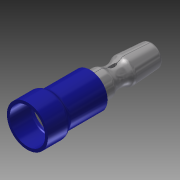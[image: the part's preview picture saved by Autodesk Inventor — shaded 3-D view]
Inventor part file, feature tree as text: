
AUTODESK INVENTOR PART (.ipt)
format: ipt  version: 2014 (Build 180170000, 170)  size: 401,408 bytes
history: native  units: in
note: dims shown in document units (in); Inventor stores cm internally (conversion verified against a paired STEP export)
features: sketch x7, projected_geometry x7, extrude x5, fillet x4, shell x2, revolve x2, plane x1, chamfer x1
ambient origin geometry x8: Origin, YZ Plane, XZ Plane, XY Plane, X Axis, Y Axis, Z Axis, Center Point
bodies: Solid1 (feature_tree), Solid2 (feature_tree)
feature tree (29):
  extrude  "Extrusion1"  Depth=0.375in TaperAngle=0.0deg
  extrude  "Extrusion2"  Depth=0.131in TaperAngle=0.0deg
  fillet  "Fillet1"  Radius=0.03in
  shell  "Shell1"  Thickness=0.017in
  revolve  "Revolution1"  Angle=90.0deg
  revolve  "Revolution2"  [1 undecoded]
  shell  "Shell2"  Thickness=0.13in
  fillet  "Fillet2"  Radius=0.179in
  fillet  "Fillet3"  Radius=0.075in
  extrude  "Extrusion3"  TaperAngle=90.0deg  [1 undecoded]
  extrude  "Extrusion4"  Depth=0.03in
  plane  "Work Plane1"
  extrude  "Extrusion5"  TaperAngle=0.0deg  [1 undecoded]
  fillet  "Fillet4"  Radius=0.002in
  chamfer  "Chamfer1"  Distance=0.0625in
  sketch  "Sketch1"  dims[d0=0.208in d1=0.375in d2=0.0in]
  sketch  "Sketch2"  dims[d3=0.245in d4=0.131in d5=0.0in d6=0.03in d7=0.017in]
  projected_geometry  "Projected Loop1"
  sketch  "Sketch3"  dims[d8=0.029in d9=90.0deg]
  sketch  "Sketch4"  dims[d10=0.373in d11=0.1525in d12=0.13in d13=0.179in d14=0.075in]
  sketch  "Sketch6"  dims[d15=0.1in d16=90.0deg]
  sketch  "Sketch7"  dims[d19=0.029in d20=0.03in]
  sketch  "Sketch8"  dims[d21=0.02in d22=0.0in d23=0.0in d24=0.002in d25=0.0in d26=0.0625in d27=0.11in d28=-0.055in d29=0.0075in d30=0.003in d31=0.125in d32=45.0deg]
  projected_geometry  "Projected Loop3"
  projected_geometry  "Project Cut Edges1"
  projected_geometry  "Project Cut Edges2"
  projected_geometry  "Project Cut Edges3"
  projected_geometry  "Project Cut Edges4"
  projected_geometry  "Project Cut Edges5"
note: 3 required parameter values undecoded (feature->parameter linkage not recoverable at this tier; creation-order binding heuristic only, values carry confidence <= 0.55)